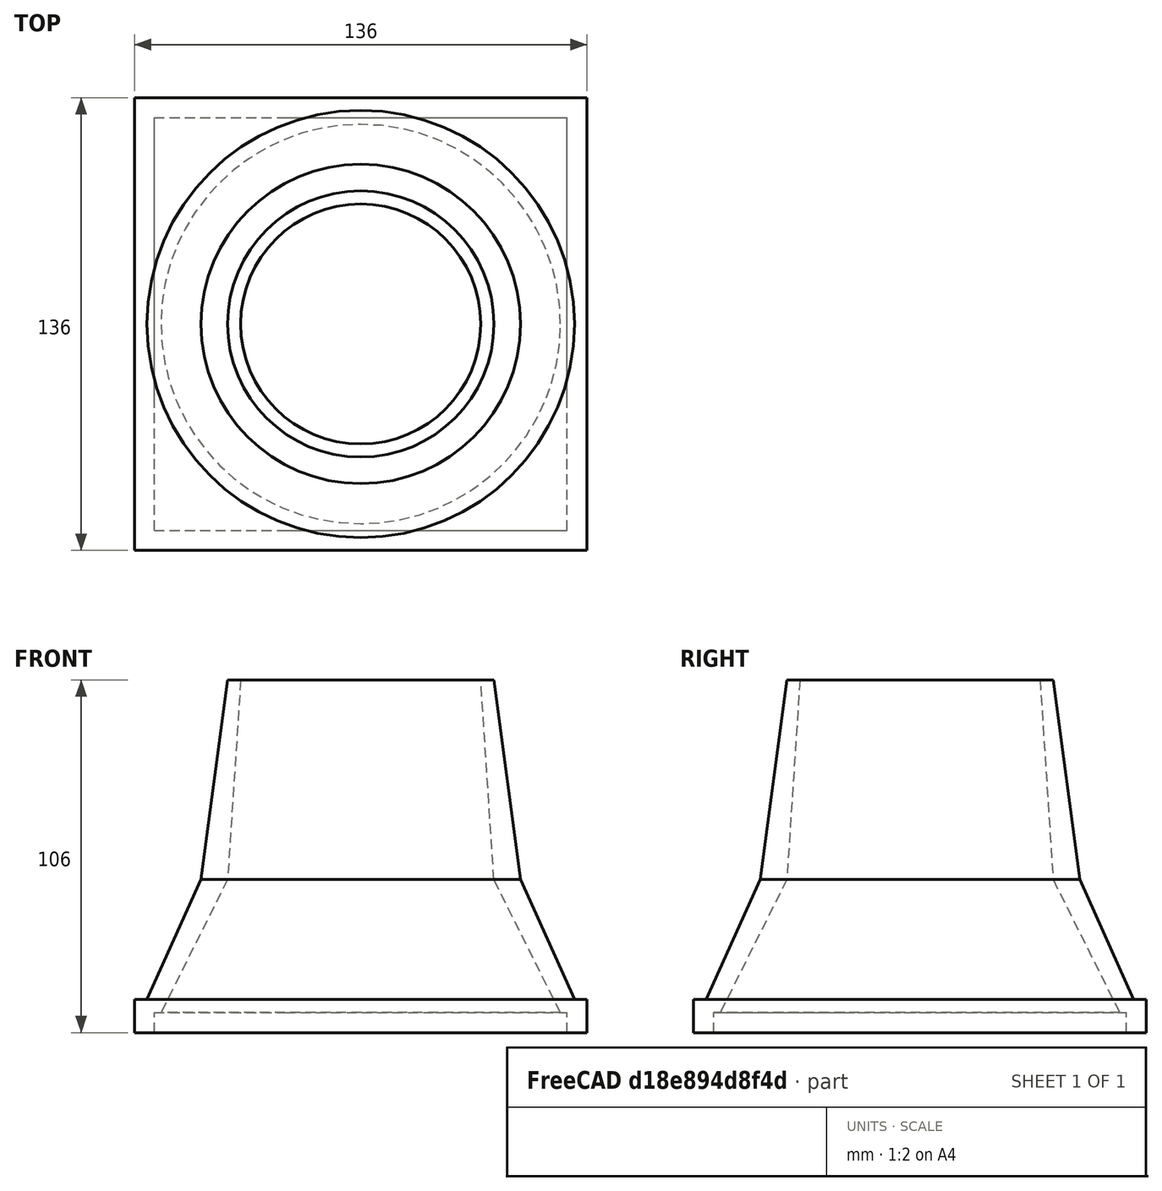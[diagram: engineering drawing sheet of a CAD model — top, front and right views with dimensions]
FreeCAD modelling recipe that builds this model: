
FCSTD DOCUMENT  (FreeCAD 0.18.4R)
Label: cowling_mk3
License: All rights reserved
LicenseURL: http://en.wikipedia.org/wiki/All_rights_reserved
objects: Part::Cone×4, Part::Cut×3, Part::Box×2, Part::Fuse×2
note: 11 computed .brp shape members not serialized (recipe doc carries the construction recipe); baked Part::Feature solids carry a one-line shape summary decoded from their .brp

FEATURE [Part::Box] Box  label="Cube"
  AttacherType = Attacher::AttachEngine3D
  Height = 10
  Length = 136
  Placement = pos=(-68,-68,0) rot=(0,0,1;0rad)
  Width = 136
FEATURE [Part::Box] Box001  label="Cube001"
  AttacherType = Attacher::AttachEngine3D
  Height = 6
  Length = 124
  Placement = pos=(-62,-62,0) rot=(0,0,1;0rad)
  Width = 124
FEATURE [Part::Cut] Cut  label="Base"
  Base = -> Box
  Tool = -> Box001
FEATURE [Part::Cone] Cone
  Angle = 360
  AttacherType = Attacher::AttachEngine3D
  Height = 40
  Placement = pos=(0,0,6) rot=(0,0,1;0rad)
  Radius1 = 66
  Radius2 = 48
FEATURE [Part::Cone] Cone001
  Angle = 360
  AttacherType = Attacher::AttachEngine3D
  Height = 40
  Placement = pos=(0,0,6) rot=(0,0,1;0rad)
  Radius1 = 60
  Radius2 = 40
FEATURE [Part::Fuse] Fusion
  Base = -> Cut
  Tool = -> Cone
FEATURE [Part::Cut] Cut001
  Base = -> Fusion
  Tool = -> Cone001
FEATURE [Part::Cone] Cone002
  Angle = 360
  AttacherType = Attacher::AttachEngine3D
  Height = 60
  Placement = pos=(0,0,46) rot=(0,0,1;0rad)
  Radius1 = 48
  Radius2 = 40
FEATURE [Part::Fuse] Fusion001
  Base = -> Cut001
  Tool = -> Cone002
FEATURE [Part::Cone] Cone003
  Angle = 360
  AttacherType = Attacher::AttachEngine3D
  Height = 61
  Placement = pos=(0,0,46) rot=(0,0,1;0rad)
  Radius1 = 40
  Radius2 = 36
FEATURE [Part::Cut] Cut002
  Base = -> Fusion001
  Tool = -> Cone003
